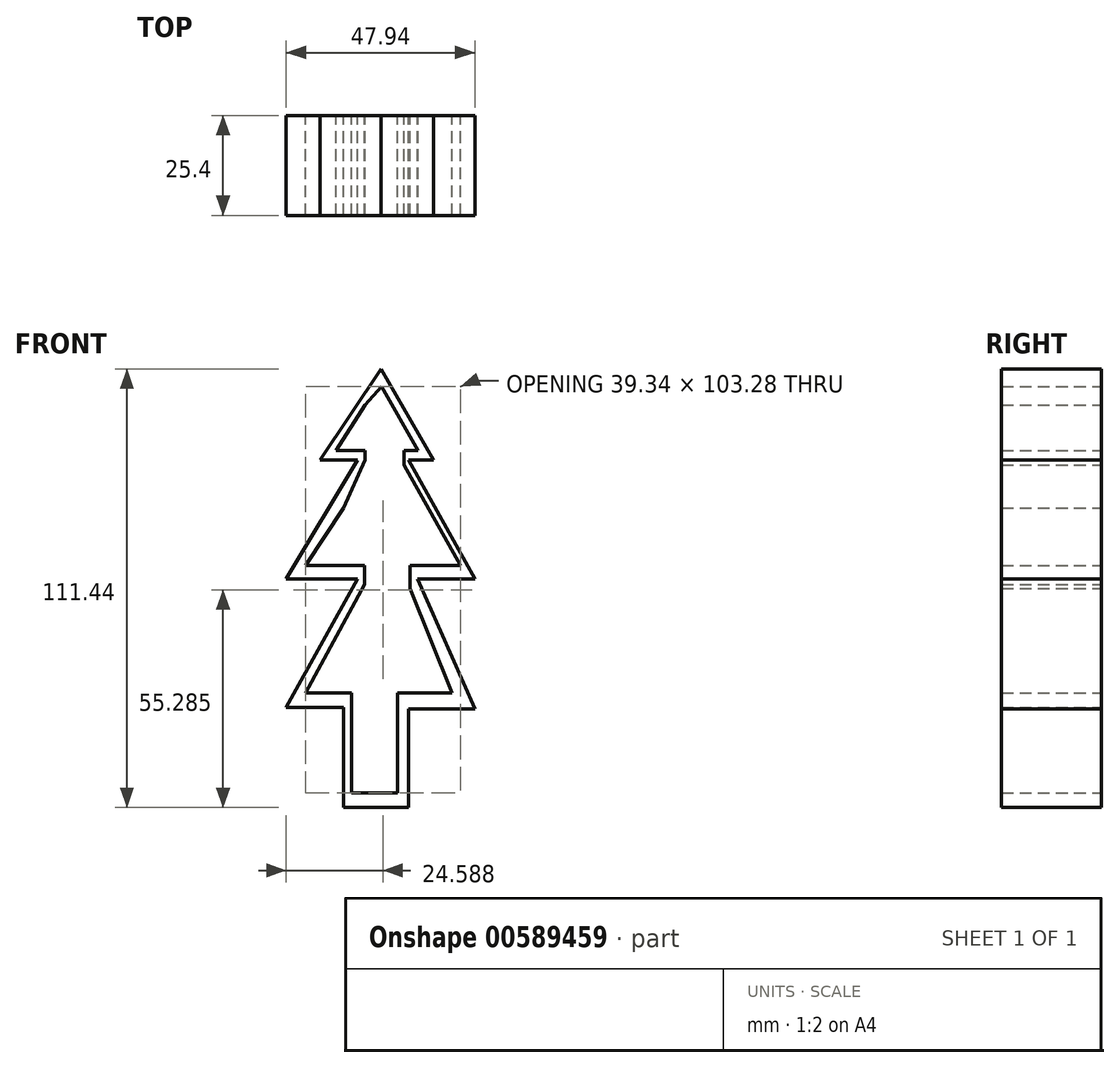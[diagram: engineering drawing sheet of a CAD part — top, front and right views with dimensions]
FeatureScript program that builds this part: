
annotation { "Feature Type Name" : "Feature", "Feature Type Description" : "" }
export const myFeature = defineFeature(function(context is Context, id is Id, definition is map)
    precondition{}
    {
        {
            var Q0;
            Q0=qCreatedBy(makeId("Front.planeOp"),FACE);
            var sketch = newSketch(context, id + "F0", { "sketchPlane" : qUnion([Q0])});
            skLineSegment(sketch, "E0", {"start": v(-13.65, -26.83) * mm, "end": v(-13.65, -52.23) * mm});
            skLineSegment(sketch, "E1", {"start": v(-13.65, -52.23) * mm, "end": v(2.86, -52.23) * mm});
            skLineSegment(sketch, "E2", {"start": v(2.86, -52.23) * mm, "end": v(2.86, -27.15) * mm});
            skLineSegment(sketch, "E3", {"start": v(2.86, -27.15) * mm, "end": v(19.68, -27.15) * mm});
            skLineSegment(sketch, "E4", {"start": v(-13.65, -26.83) * mm, "end": v(-28.26, -26.83) * mm});
            skLineSegment(sketch, "E5", {"start": v(-28.26, -26.83) * mm, "end": v(-10.16, 5.87) * mm});
            skLineSegment(sketch, "E6", {"start": v(19.68, -27.15) * mm, "end": v(5.08, 5.87) * mm});
            skLineSegment(sketch, "E7", {"start": v(-10.16, 5.87) * mm, "end": v(-28.26, 5.87) * mm});
            skLineSegment(sketch, "E8", {"start": v(5.08, 5.87) * mm, "end": v(19.68, 5.87) * mm});
            skLineSegment(sketch, "E9", {"start": v(19.68, 5.87) * mm, "end": v(2.86, 36.04) * mm});
            skLineSegment(sketch, "E10", {"start": v(-28.26, 5.87) * mm, "end": v(-10.16, 36.04) * mm});
            skLineSegment(sketch, "E11", {"start": v(-10.16, 36.04) * mm, "end": v(-19.69, 36.04) * mm});
            skLineSegment(sketch, "E12", {"start": v(-19.69, 36.04) * mm, "end": v(-4.13, 59.21) * mm});
            skLineSegment(sketch, "E13", {"start": v(-4.13, 59.21) * mm, "end": v(9.2, 36.04) * mm});
            skLineSegment(sketch, "E14", {"start": v(9.2, 36.04) * mm, "end": v(2.86, 36.04) * mm});
            skLineSegment(sketch, "E15", {"start": v(-13.65, 23.9) * mm, "end": v(-23.34, 9.32) * mm});
            skLineSegment(sketch, "E16", {"start": v(-23.34, 9.32) * mm, "end": v(-8.31, 9.32) * mm});
            skLineSegment(sketch, "E17", {"start": v(-8.31, 9.32) * mm, "end": v(-8.31, 4.45) * mm});
            skLineSegment(sketch, "E18", {"start": v(-8.31, 4.45) * mm, "end": v(-23.34, -23.12) * mm});
            skLineSegment(sketch, "E19", {"start": v(-23.34, -23.12) * mm, "end": v(-11.6, -23.12) * mm});
            skLineSegment(sketch, "E20", {"start": v(-11.6, -23.12) * mm, "end": v(-11.6, -48.58) * mm});
            skLineSegment(sketch, "E21", {"start": v(-11.6, -48.58) * mm, "end": v(0, -48.58) * mm});
            skLineSegment(sketch, "E22", {"start": v(0, -48.58) * mm, "end": v(0, -23.12) * mm});
            skLineSegment(sketch, "E23", {"start": v(0, -23.12) * mm, "end": v(13.84, -23.12) * mm});
            skLineSegment(sketch, "E24", {"start": v(13.84, -23.12) * mm, "end": v(3.14, 3.4) * mm});
            skLineSegment(sketch, "E25", {"start": v(3.14, 3.4) * mm, "end": v(3.14, 9.22) * mm});
            skLineSegment(sketch, "E26", {"start": v(3.14, 9.22) * mm, "end": v(16, 9.22) * mm});
            skLineSegment(sketch, "E27", {"start": v(16, 9.22) * mm, "end": v(1.7, 34.84) * mm});
            skLineSegment(sketch, "E28", {"start": v(-13.65, 23.9) * mm, "end": v(-8.2, 36.04) * mm});
            skLineSegment(sketch, "E29", {"start": v(1.7, 34.84) * mm, "end": v(1.7, 38.46) * mm});
            skLineSegment(sketch, "E30", {"start": v(1.7, 38.46) * mm, "end": v(5.28, 38.46) * mm});
            skLineSegment(sketch, "E31", {"start": v(5.28, 38.46) * mm, "end": v(-4.06, 54.7) * mm});
            skLineSegment(sketch, "E32", {"start": v(-8.2, 36.04) * mm, "end": v(-8.2, 38.46) * mm});
            skPoint(sketch, "E32.endSnap0", {"position": v(3.5, 38.46) * mm});
            skLineSegment(sketch, "E33", {"start": v(-8.2, 38.46) * mm, "end": v(-15.56, 38.46) * mm});
            skLineSegment(sketch, "E34", {"start": v(-15.56, 38.46) * mm, "end": v(-8.2, 50.05) * mm});
            skLineSegment(sketch, "E35", {"start": v(-8.2, 50.05) * mm, "end": v(-4.06, 54.7) * mm});
            skSolve(sketch);
        }
        {
            var Q0;
            Q0 = qSketchRegion(id + "F0", true);
            extrude(context, id + "F1", {"entities" : qUnion([Q0]), "depth" : 25.4 * mm, "offsetDistance" : 25.4 * mm});
        }
    });
